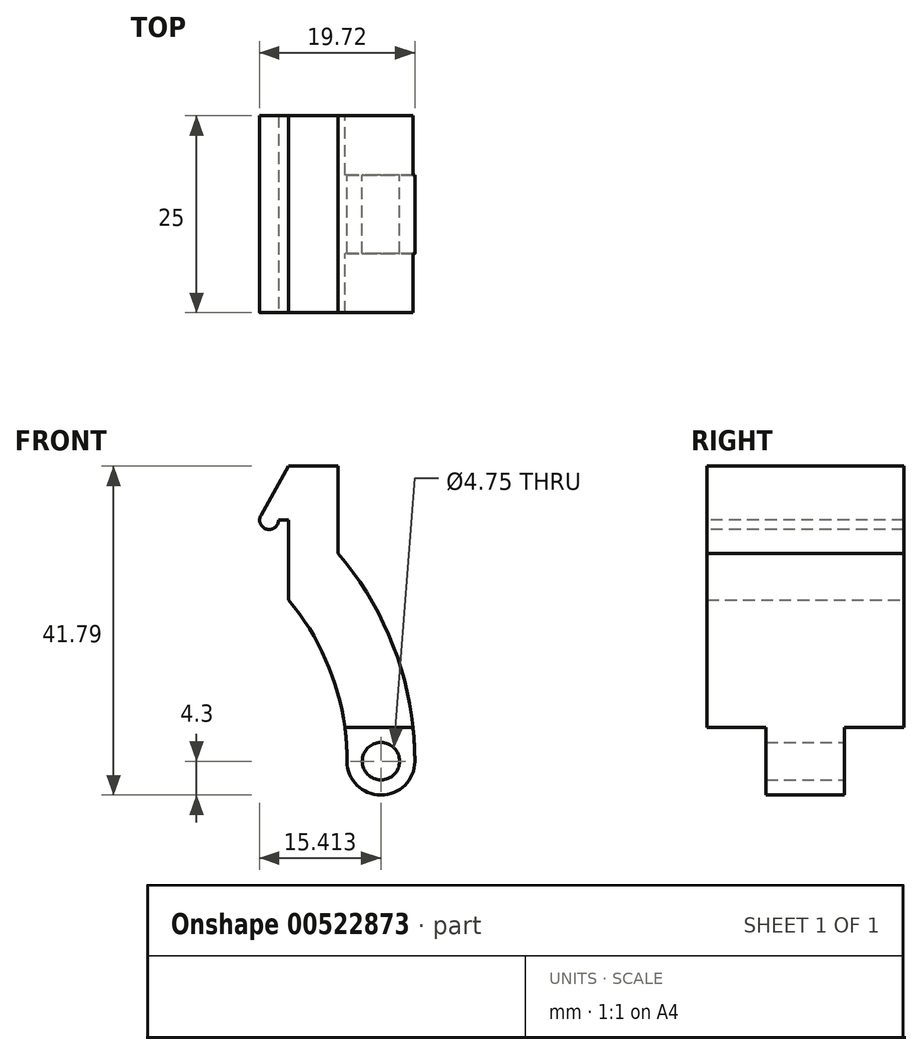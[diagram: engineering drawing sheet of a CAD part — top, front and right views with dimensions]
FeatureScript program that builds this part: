
annotation { "Feature Type Name" : "Feature", "Feature Type Description" : "" }
export const myFeature = defineFeature(function(context is Context, id is Id, definition is map)
    precondition{}
    {
        {
            var Q0;
            Q0=qCreatedBy(makeId("Front.planeOp"),FACE);
            var sketch = newSketch(context, id + "F0", { "sketchPlane" : qUnion([Q0])});
            skLineSegment(sketch, "E0.bottom", {"start": v(-25.4, 40.62) * mm, "end": v(24.6, 40.62) * mm});
            skLineSegment(sketch, "E0.left", {"start": v(-25.4, 40.62) * mm, "end": v(-25.4, 31.71) * mm});
            skLineSegment(sketch, "E0.right", {"start": v(24.6, 40.62) * mm, "end": v(24.6, 32.32) * mm});
            skPoint(sketch, "E0.middle", {"position": v(0, 0) * mm});
            skArc(sketch, "E1", {"start": v(-25.4, 31.71) * mm, "mid": v(0.5, -40.62) * mm, "end": v(24.6, 32.32) * mm});
            skCircle(sketch, "E2", {"center": v(0, 0) * mm, "radius": 32.02 * mm});
            skLineSegment(sketch, "E3", {"start": v(32.02, 0) * mm, "end": v(40.62, 0) * mm});
            skCircle(sketch, "E4", {"center": v(36.32, 0) * mm, "radius": 2.38 * mm});
            skCircle(sketch, "E5", {"center": v(36.32, 0) * mm, "radius": 4.3 * mm});
            skLineSegment(sketch, "E6", {"start": v(24.6, 32.32) * mm, "end": v(24.6, 20.49) * mm});
            skLineSegment(sketch, "E7", {"start": v(36.32, 4.3) * mm, "end": v(31.73, 4.3) * mm});
            skLineSegment(sketch, "E8", {"start": v(36.32, 4.3) * mm, "end": v(40.4, 4.3) * mm});
            skSolve(sketch);
        }
        {
            var Q0;
            {var subQ0=sQuery(id+"F0.wireOp",EDGE,"E6");Q0=makeQuery(id+"F0.imprint","IMPRINT",FACE,{"disambiguationData":[TD([[makeQuery(id+"F0.imprint","IMPRINT",EDGE,{"derivedFrom":subQ0}),1.0]])]});}
            var Q1;
            {var subQ1=sQuery(id+"F0.wireOp",EDGE,"E3");var subQ3=sQuery(id+"F0.wireOp",EDGE,"E4");var subQ4=makeQuery(id+"F0.imprint","INTERSECT",VERTEX,{"disambiguationData":[OD(0.0)],"derivedFrom":[subQ1,subQ3]});Q1=makeQuery(id+"F0.imprint","IMPRINT",FACE,{"disambiguationData":[TD([[makeQuery(id+"F0.imprint","IMPRINT",EDGE,{"disambiguationData":[TD([[subQ4,1.0]])],"derivedFrom":subQ3}),-1.0]])]});}
            var Q2;
            {var subQ1=sQuery(id+"F0.wireOp",EDGE,"E3");var subQ3=sQuery(id+"F0.wireOp",EDGE,"E4");var subQ4=makeQuery(id+"F0.imprint","INTERSECT",VERTEX,{"disambiguationData":[OD(0.0)],"derivedFrom":[subQ1,subQ3]});Q2=makeQuery(id+"F0.imprint","IMPRINT",FACE,{"disambiguationData":[TD([[makeQuery(id+"F0.imprint","IMPRINT",EDGE,{"disambiguationData":[TD([[subQ4,-1.0]])],"derivedFrom":subQ3}),-1.0]])]});}
            var Q3;
            {var subQ3=sQuery(id+"F0.wireOp",EDGE,"E7");Q3=makeQuery(id+"F0.imprint","IMPRINT",FACE,{"disambiguationData":[TD([[makeQuery(id+"F0.imprint","IMPRINT",EDGE,{"derivedFrom":subQ3}),1.0]])]});}
            var Q4;
            {var subQ3=sQuery(id+"F0.wireOp",EDGE,"E8");Q4=makeQuery(id+"F0.imprint","IMPRINT",FACE,{"disambiguationData":[TD([[makeQuery(id+"F0.imprint","IMPRINT",EDGE,{"derivedFrom":subQ3}),-1.0]])]});}
            extrude(context, id + "F1", {"entities" : qUnion([Q0, Q1, Q2, Q3, Q4]), "endBound" : BoundingType.SYMMETRIC, "depth" : 10 * mm, "offsetDistance" : 25 * mm});
        }
        {
            var Q0;
            {var subQ1=sQuery(id+"F0.wireOp",EDGE,"E6");Q0=makeQuery(id+"F0.imprint","IMPRINT",FACE,{"disambiguationData":[TD([[makeQuery(id+"F0.imprint","IMPRINT",EDGE,{"derivedFrom":subQ1}),1.0]])]});}
            extrude(context, id + "F2", {"entities" : qUnion([Q0]), "operationType" : NewBodyOperationType.ADD, "endBound" : BoundingType.SYMMETRIC, "depth" : 25 * mm, "offsetDistance" : 25 * mm});
        }
        {
            var Q0;
            Q0=makeQuery(id+"F2.opExtrude","CAP_FACE",FACE,{"disambiguationData":[OSD([sQuery(id+"F0.wireOp",EDGE,"E1"),sQuery(id+"F0.wireOp",EDGE,"E2"),sQuery(id+"F0.wireOp",EDGE,"E6"),sQuery(id+"F0.wireOp",EDGE,"E7"),sQuery(id+"F0.wireOp",EDGE,"E8")])],"isStart":false});
            var sketch = newSketch(context, id + "F3", { "sketchPlane" : qUnion([Q0])});
            skLineSegment(sketch, "E9.bottom", {"start": v(24.6, 20.49) * mm, "end": v(30.87, 20.49) * mm});
            skLineSegment(sketch, "E9.top", {"start": v(24.6, 37.49) * mm, "end": v(30.87, 37.49) * mm});
            skLineSegment(sketch, "E9.left", {"start": v(24.6, 20.49) * mm, "end": v(24.6, 37.49) * mm});
            skLineSegment(sketch, "E9.right", {"start": v(30.87, 20.49) * mm, "end": v(30.87, 37.49) * mm});
            skLineSegment(sketch, "E10", {"start": v(24.6, 20.49) * mm, "end": v(24.6, 30.64) * mm});
            skLineSegment(sketch, "E11", {"start": v(24.6, 30.64) * mm, "end": v(22.1, 30.64) * mm});
            skCircle(sketch, "E12", {"center": v(22.1, 30.64) * mm, "radius": 1.2 * mm});
            skLineSegment(sketch, "E13", {"start": v(24.6, 37.49) * mm, "end": v(21.07, 31.23) * mm});
            skSolve(sketch);
        }
        {
            var Q0;
            Q0 = qSketchRegion(id + "F3", true);
            extrude(context, id + "F4", {"entities" : qUnion([Q0]), "operationType" : NewBodyOperationType.ADD, "oppositeDirection" : true, "depth" : 25 * mm, "offsetDistance" : 25 * mm});
        }
    });
